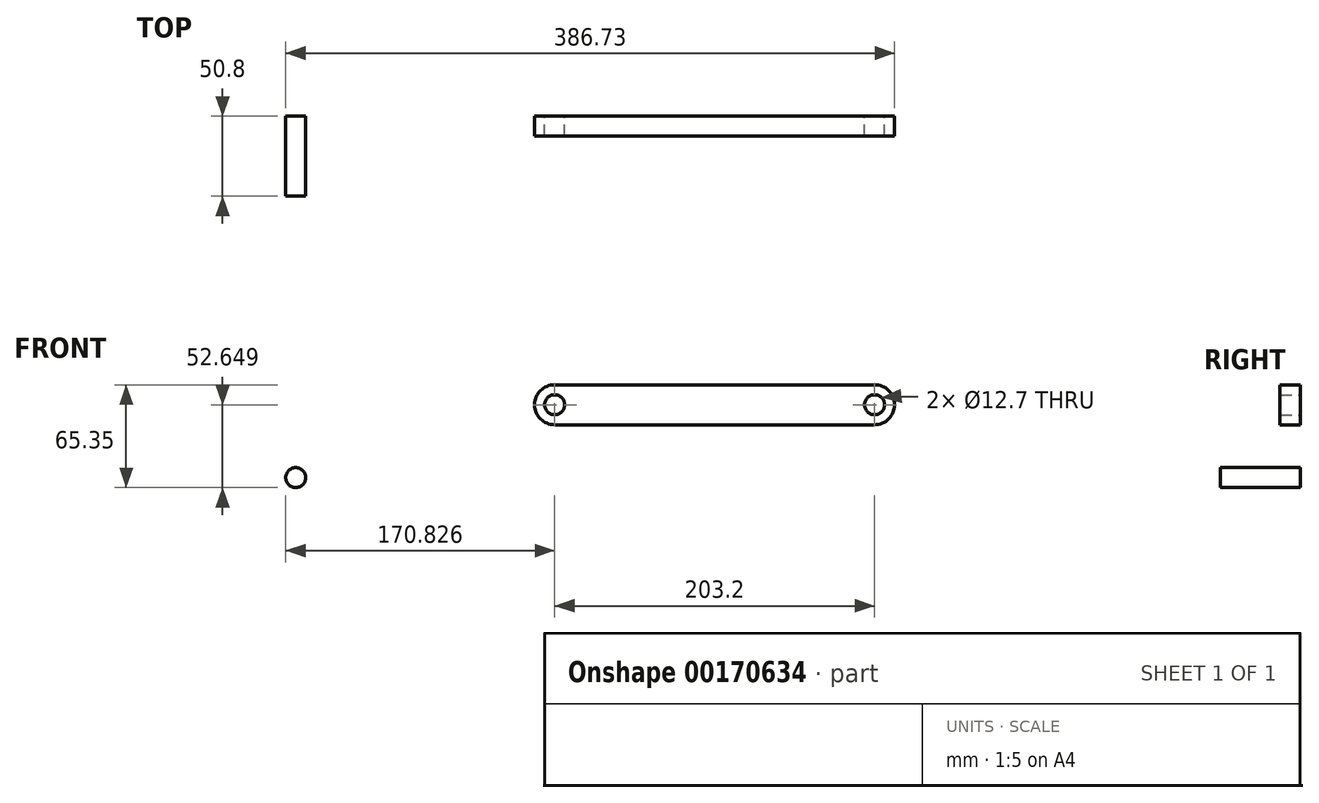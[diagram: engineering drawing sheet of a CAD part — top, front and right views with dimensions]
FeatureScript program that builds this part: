
annotation { "Feature Type Name" : "Feature", "Feature Type Description" : "" }
export const myFeature = defineFeature(function(context is Context, id is Id, definition is map)
    precondition{}
    {
        {
            var Q0;
            Q0=qCreatedBy(makeId("Front.planeOp"),FACE);
            var sketch = newSketch(context, id + "F0", { "sketchPlane" : qUnion([Q0])});
            skLineSegment(sketch, "E0.bottom", {"start": v(-102.2, 8.99) * mm, "end": v(101, 8.99) * mm});
            skLineSegment(sketch, "E0.top", {"start": v(-102.2, -16.41) * mm, "end": v(101, -16.41) * mm});
            skLineSegment(sketch, "E0.left", {"start": v(-102.2, 8.99) * mm, "end": v(-102.2, -16.41) * mm});
            skLineSegment(sketch, "E0.right", {"start": v(101, 8.99) * mm, "end": v(101, -16.41) * mm});
            skArc(sketch, "E1", {"start": v(101, -16.41) * mm, "mid": v(113.7, -3.71) * mm, "end": v(101, 8.99) * mm});
            skCircle(sketch, "E2", {"center": v(101, -3.71) * mm, "radius": 6.35 * mm});
            skArc(sketch, "E3", {"start": v(-102.2, 8.99) * mm, "mid": v(-114.9, -3.71) * mm, "end": v(-102.2, -16.41) * mm});
            skCircle(sketch, "E4", {"center": v(-102.2, -3.71) * mm, "radius": 6.35 * mm});
            skSolve(sketch);
        }
        {
            var Q0;
            {var subQ5=sQuery(id+"F0.wireOp",EDGE,"E0.bottom");Q0=makeQuery(id+"F0.imprint","IMPRINT",FACE,{"disambiguationData":[TD([[makeQuery(id+"F0.imprint","IMPRINT",EDGE,{"derivedFrom":subQ5}),-1.0]])]});}
            var Q1;
            {var subQ0=sQuery(id+"F0.wireOp",EDGE,"E3");Q1=makeQuery(id+"F0.imprint","IMPRINT",FACE,{"disambiguationData":[TD([[makeQuery(id+"F0.imprint","IMPRINT",EDGE,{"derivedFrom":subQ0}),1.0]])]});}
            var Q2;
            {var subQ0=sQuery(id+"F0.wireOp",EDGE,"E1");Q2=makeQuery(id+"F0.imprint","IMPRINT",FACE,{"disambiguationData":[TD([[makeQuery(id+"F0.imprint","IMPRINT",EDGE,{"derivedFrom":subQ0}),1.0]])]});}
            extrude(context, id + "F1", {"entities" : qUnion([Q0, Q1, Q2]), "depth" : 12.7 * mm});
        }
        {
            var Q0;
            Q0=qCreatedBy(makeId("Front.planeOp"),FACE);
            var sketch = newSketch(context, id + "F2", { "sketchPlane" : qUnion([Q0])});
            skCircle(sketch, "E5", {"center": v(-266.68, -50.01) * mm, "radius": 6.35 * mm});
            skCircle(sketch, "E6", {"center": v(-372.61, 11.27) * mm, "radius": 6.25 * mm});
            skSolve(sketch);
        }
        {
            var Q0;
            Q0=makeQuery(id+"F2.imprint","IMPRINT",FACE,{"disambiguationData":[TD([[makeQuery(id+"F2.imprint","IMPRINT",EDGE,{"derivedFrom":sQuery(id+"F2.wireOp",EDGE,"E5")}),1.0]])]});
            extrude(context, id + "F3", {"entities" : qUnion([Q0]), "depth" : 50.8 * mm});
        }
    });
